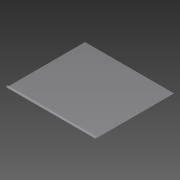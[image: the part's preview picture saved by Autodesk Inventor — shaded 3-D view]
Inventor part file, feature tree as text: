
AUTODESK INVENTOR PART (.ipt)
format: ipt  version: 2013 (Build 170138000, 138)  size: 99,840 bytes
history: native  units: in
note: dims shown in document units (in); Inventor stores cm internally (conversion verified against a paired STEP export)
features: sheet_metal_op x7, sketch x3, other x3
ambient origin geometry x8: Origin, YZ Plane, XZ Plane, XY Plane, X Axis, Y Axis, Z Axis, Center Point
bodies: Solid1 (feature_tree)
feature tree (13):
  sheet_metal_op  "Face1"
  sheet_metal_op  "Flange1"
  sheet_metal_op  "Flange2"
  sketch  "Sketch1"  dims[d0=54.0in]
  other  "Plate1"
  sketch  "Sketch2"  dims[d1=48.0in]
  other  "Plate2"
  sheet_metal_op  "Bend1"
  sheet_metal_op  "Corner1"
  sketch  "Sketch3"  dims[d2=0.2125in d3=0.2125in d4=0.1063in d5=0.425in d6=0.2125in d7=1.0in d8=90.0deg d9=0.2125in d10=0.85in d11=0.2125in d12=0.2125in d13=0.2125in d14=0.1063in d15=0.425in d16=0.2125in d17=1.0in d18=90.0deg d19=0.2125in d20=0.85in d21=0.2125in d22=0.2125in]
  other  "Plate3"
  sheet_metal_op  "Bend2"
  sheet_metal_op  "Corner2"
